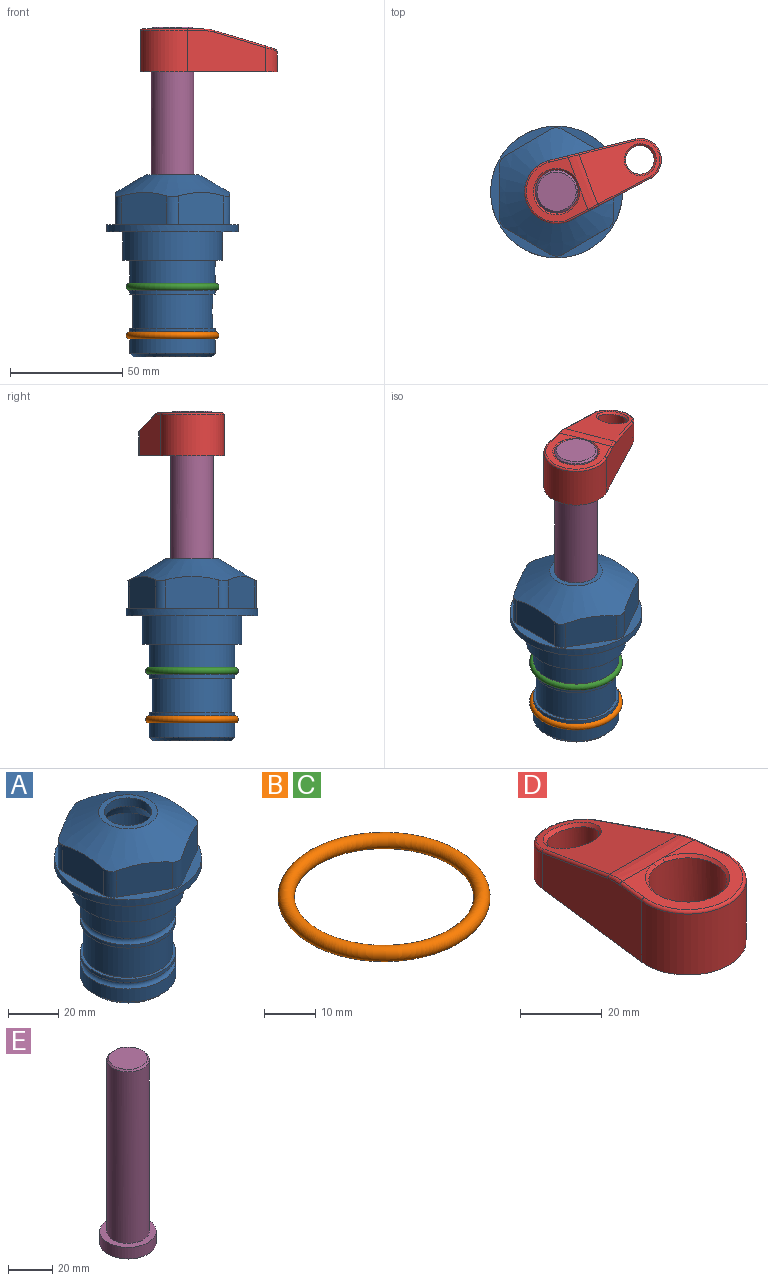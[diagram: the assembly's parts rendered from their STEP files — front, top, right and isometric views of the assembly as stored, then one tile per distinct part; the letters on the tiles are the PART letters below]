
ASSEMBLY  parts=5 mates=4
PART A: 36 faces, bbox 58.7x58.7x81 mm
  f0: cylinder r=17.78mm len=35.56mm, axis (0,0,1), area 1670.8mm2, adj f23,f24,f31
  f1: cylinder r=19.05mm len=38.1mm, axis (0,0,1), area 1191.9mm2, adj f26,f27,f30
  f2: plane 58.66x58.66mm, normal (0,0,-1), area 1150.6mm2, adj f3,f28
  f3: cylinder r=29.33mm len=58.66mm, axis (0,0,-1), area 585.1mm2, adj f2,f4
  f4: plane 58.66x58.66mm, normal (0,0,1), area 475.9mm2, adj f3,f5,f6,f7,f8,f9,f10,f11
  f5: plane 20.32x14.34mm, normal (-0.5,0.87,0), area 324.4mm2, adj f4,f15,f16,f17
  f6: plane 20.32x14.34mm, normal (0.5,0.87,0), area 324.4mm2, adj f4,f14,f15,f17
  f7: plane 23.48x14.34mm, normal (1,0,0), area 324.4mm2, adj f4,f13,f14,f17
  f8: plane 20.32x14.34mm, normal (0.5,-0.87,0), area 324.4mm2, adj f4,f12,f13,f17
  f9: plane 20.32x14.34mm, normal (-0.5,-0.87,0), area 324.4mm2, adj f4,f11,f12,f17
  f10: plane 23.48x14.34mm, normal (-1,0,0), area 324.4mm2, adj f4,f11,f16,f17
  f11: cylinder r=5.08mm len=12.85mm, axis (0,0,-1), area 67.2mm2, adj f4,f9,f10,f17
  f12: cylinder r=5.08mm len=12.85mm, axis (0,0,-1), area 67.2mm2, adj f4,f8,f9,f17
  f13: cylinder r=5.08mm len=12.85mm, axis (0,0,-1), area 67.2mm2, adj f4,f7,f8,f17
  f14: cylinder r=5.08mm len=12.85mm, axis (0,0,-1), area 67.2mm2, adj f4,f6,f7,f17
  f15: cylinder r=5.08mm len=12.85mm, axis (0,0,-1), area 67.2mm2, adj f4,f5,f6,f17
  f16: cylinder r=5.08mm len=12.85mm, axis (0,0,-1), area 67.2mm2, adj f4,f5,f10,f17
  f17: cone r=11.73mm half-angle=60deg, axis (0,0,-1), area 2071.8mm2, adj f5,f6,f7,f8,f9,f10,f11,f12
  f18: plane 23.46x23.46mm, normal (0,0,1), area 147.4mm2, adj f17,f35
  f19: plane 34.93x34.93mm, normal (0,0,-1), area 958mm2, adj f29
  f20: cylinder r=19.05mm len=38.1mm, axis (0,0,1), area 760.1mm2, adj f21,f29
  f21: torus R=19.05mm, axis (0,0,1), area 565.3mm2, adj f20,f22
  f22: cylinder r=19.05mm len=38.1mm, axis (0,0,1), area 190mm2, adj f21,f23
  f23: plane 38.1x38.1mm, normal (0,0,1), area 146.9mm2, adj f0,f22
  f24: plane 38.1x38.1mm, normal (0,0,-1), area 146.9mm2, adj f0,f25
  f25: cylinder r=19.05mm len=38.1mm, axis (0,0,1), area 190mm2, adj f24,f26
  f26: torus R=19.05mm, axis (0,0,1), area 565.3mm2, adj f1,f25
  f27: plane 44.45x44.45mm, normal (0,0,-1), area 411.7mm2, adj f1,f28
  f28: cylinder r=22.23mm len=44.45mm, axis (0,0,1), area 1773.5mm2, adj f2,f27
  f29: cone r=19.05mm half-angle=45deg, axis (0,0,1), area 257.5mm2, adj f19,f20
  f30: cylinder r=3.17mm len=6.75mm, axis (-1,0,0), area 128mm2, adj f1,f33
  f31: cylinder r=3.17mm len=6.35mm, axis (-1,0,0), area 102.5mm2, adj f0,f33
  f32: plane 25.4x25.4mm, normal (0,0,1), area 506.7mm2, adj f33
  f33: cylinder r=12.7mm len=66.42mm, axis (0,0,-1), area 5236.2mm2, adj f30,f31,f32,f34
  f34: cone r=9.53mm half-angle=30deg, axis (0,0,-1), area 443.4mm2, adj f33,f35
  f35: cylinder r=9.53mm len=19.05mm, axis (0,0,-1), area 240.9mm2, adj f18,f34
PART B: 1 faces, bbox 44.7x44.7x3.2 mm
  f0: torus R=19.05mm, axis (0,0,1), area 1193.9mm2
PART C: same geometry as B
PART D: 31 faces, bbox 31.7x65.5x19.8 mm
  f0: plane 39.12x18.26mm, normal (0.99,0.12,0), area 612.2mm2, adj f1,f4,f7,f11,f13,f15
  f1: cylinder r=9.53mm len=18.91mm, axis (0,0,-1), area 296.1mm2, adj f0,f2,f7,f17
  f2: plane 39.12x18.26mm, normal (-0.99,0.12,0), area 612.2mm2, adj f1,f4,f7,f12,f14,f16
  f3: cylinder r=6.35mm len=12.7mm, axis (0,0,-1), area 362.4mm2, adj f7,f18
  f4: cylinder r=14.29mm len=28.58mm, axis (0,0,-1), area 882.2mm2, adj f0,f2,f7,f10
  f5: cylinder r=9.53mm len=19.05mm, axis (0,0,-1), area 1092.6mm2, adj f7,f19,f20
  f6: plane 26.99x23.69mm, normal (0,0,1), area 216.2mm2, adj f9,f10,f11,f12,f19
  f7: plane 63.5x28.58mm, normal (0,0,-1), area 661.8mm2, adj f0,f1,f2,f3,f4,f5,f22,f23
  f8: plane 33.52x23.6mm, normal (0,0.26,0.97), area 486mm2, adj f9,f15,f16,f17,f18
  f9: cylinder r=19.05mm len=24.72mm, axis (1,0,0), area 120.4mm2, adj f6,f8,f13,f14,f20
  f10: torus R=13.49mm, axis (0,0,1), area 59mm2, adj f4,f6,f11,f12
  f11: cylinder r=0.79mm len=8.67mm, axis (0.12,-0.99,0), area 10.8mm2, adj f0,f6,f10,f13
  f12: cylinder r=0.79mm len=8.67mm, axis (0.12,0.99,0), area 10.8mm2, adj f2,f6,f10,f14
  f13: bspline ~4.95x1.42mm, area 6.1mm2, adj f0,f9,f11,f15
  f14: bspline ~4.95x1.42mm, area 6.1mm2, adj f2,f9,f12,f16
  f15: cylinder r=0.79mm len=25.95mm, axis (0.12,-0.96,0.26), area 32.9mm2, adj f0,f8,f13,f17
  f16: cylinder r=0.79mm len=25.95mm, axis (0.12,0.96,-0.26), area 32.9mm2, adj f2,f8,f14,f17
  f17: bspline ~18.91x8.38mm, area 30mm2, adj f1,f8,f15,f16
  f18: bspline ~14.29x14.29mm, area 48.3mm2, adj f3,f8
  f19: cone r=9.53mm half-angle=45deg, axis (0,0,1), area 66.5mm2, adj f5,f6,f20
  f20: bspline ~3.22x0.96mm, area 3.5mm2, adj f5,f9,f19
  f21: plane 2.75x2.72mm, normal (0,0,-1), area 2.9mm2, adj f23,f25,f28
  f22: plane 23.05x15.88mm, normal (-0.99,-0.12,0), area 323.6mm2, adj f7,f25,f26,f27,f28,f29
  f23: plane 23.05x15.88mm, normal (0.99,-0.12,0), area 323.6mm2, adj f7,f21,f25,f27,f28,f30
  f24: cylinder r=9.53mm len=10.69mm, axis (0,0,-1), area 114.7mm2, adj f7,f27,f29,f30
  f25: cylinder r=12.7mm len=20.59mm, axis (0,0,-1), area 381.1mm2, adj f7,f21,f22,f23,f26,f28
  f26: plane 2.75x2.72mm, normal (0,0,-1), area 2.9mm2, adj f22,f25,f28
  f27: plane 19.72x18.37mm, normal (0,-0.26,-0.97), area 291.8mm2, adj f22,f23,f24,f28,f29,f30
  f28: cylinder r=15.88mm len=19.92mm, axis (1,0,0), area 54.8mm2, adj f21,f22,f23,f25,f26,f27
  f29: cylinder r=1.59mm len=11mm, axis (0,0,-1), area 34.7mm2, adj f7,f22,f24,f27
  f30: cylinder r=1.59mm len=11mm, axis (0,0,-1), area 34.7mm2, adj f7,f23,f24,f27
PART E: 6 faces, bbox 25.4x25.4x101.6 mm
  f0: plane 17.46x17.46mm, normal (0,0,1), area 239.5mm2, adj f5
  f1: plane 25.4x25.4mm, normal (0,0,-1), area 506.7mm2, adj f2
  f2: cylinder r=12.7mm len=25.4mm, axis (0,0,1), area 506.7mm2, adj f1,f3
  f3: plane 25.4x25.4mm, normal (0,0,1), area 221.7mm2, adj f2,f4
  f4: cylinder r=9.53mm len=94.46mm, axis (0,0,1), area 5653mm2, adj f3,f5
  f5: cone r=8.73mm half-angle=45deg, axis (0,0,-1), area 64.4mm2, adj f0,f4
PLACE A at identity fixed
PLACE B t=(0,0,-21.59)mm
PLACE C at identity
PLACE D rot(axis=(0,0,-1),69.1deg) t=(0,0,26.76)mm
PLACE E rot(axis=(0,0,-1),69.1deg) t=(0,0,27.55)mm
MATE fastened E.f2 <-> D.f4  axis (0,0,1) through (0,0,90.26)mm
MATE fastened A.f0 <-> B.f0  axis (0,0,1) through (0,0,-46.1)mm
MATE fastened A.f0 <-> C.f0  axis (0,0,1) through (0,0,-24.51)mm
MATE cylindrical A.f0 <-> E.f2  axis (0,0,1) through (0,0,-50.55)mm
